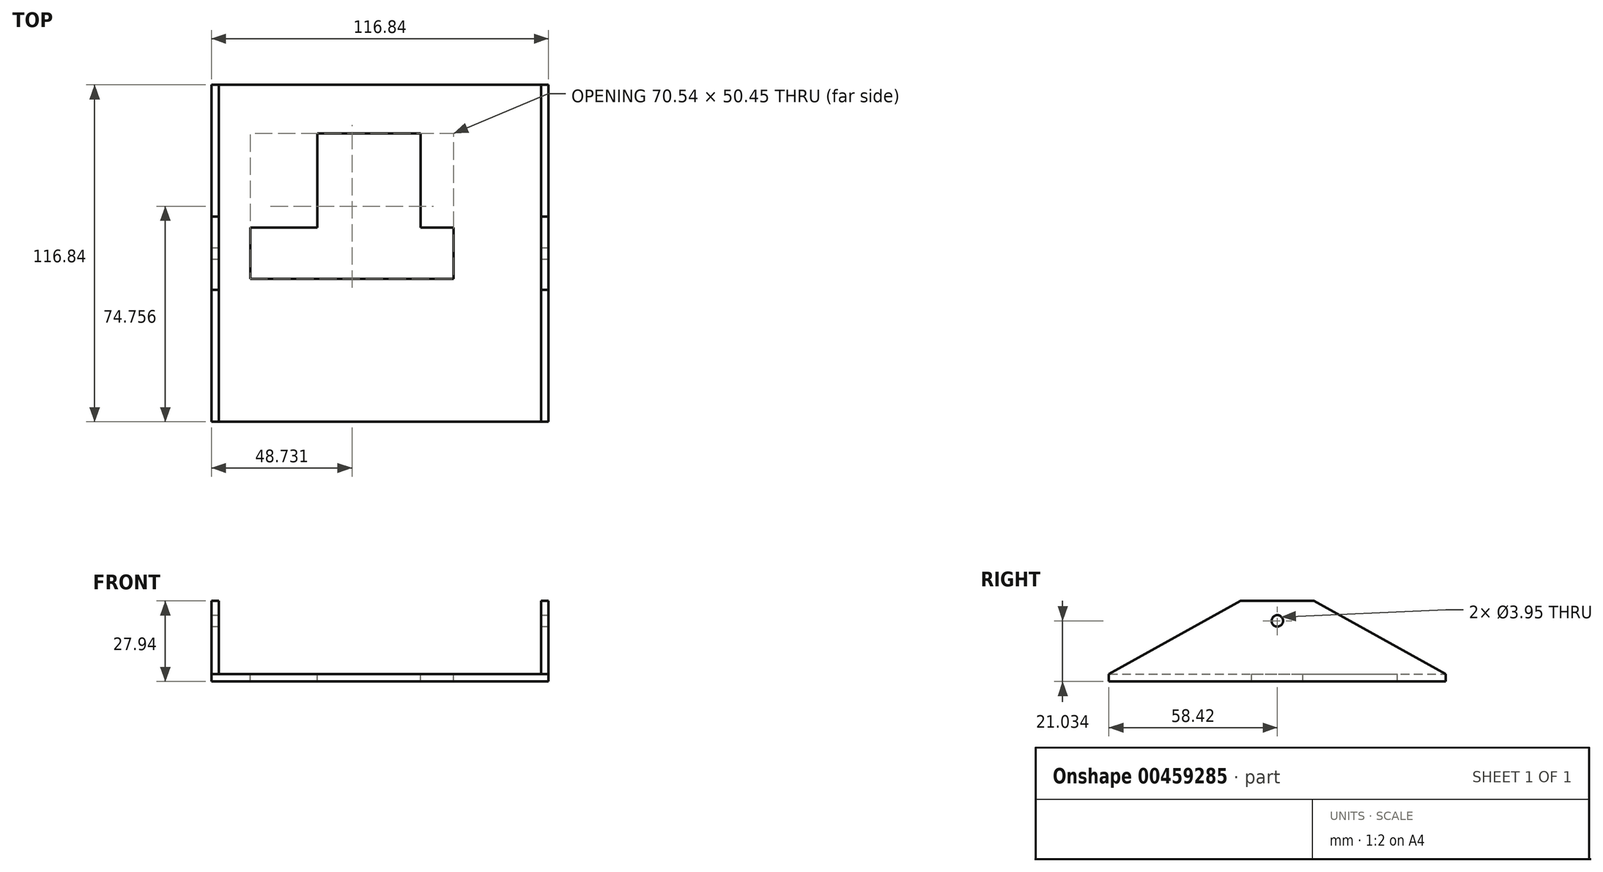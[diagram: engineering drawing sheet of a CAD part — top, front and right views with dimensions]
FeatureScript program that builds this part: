
annotation { "Feature Type Name" : "Feature", "Feature Type Description" : "" }
export const myFeature = defineFeature(function(context is Context, id is Id, definition is map)
    precondition{}
    {
        {
            var Q0;
            Q0=qCreatedBy(makeId("Top.planeOp"),FACE);
            var sketch = newSketch(context, id + "F0", { "sketchPlane" : qUnion([Q0])});
            skLineSegment(sketch, "E0.bottom", {"start": v(58.42, -58.42) * mm, "end": v(-58.42, -58.42) * mm});
            skLineSegment(sketch, "E0.top", {"start": v(58.42, 58.42) * mm, "end": v(-58.42, 58.42) * mm});
            skLineSegment(sketch, "E0.left", {"start": v(58.42, -58.42) * mm, "end": v(58.42, 58.42) * mm});
            skLineSegment(sketch, "E0.right", {"start": v(-58.42, -58.42) * mm, "end": v(-58.42, 58.42) * mm});
            skPoint(sketch, "E0.middle", {"position": v(0, 0) * mm});
            skSolve(sketch);
        }
        {
            var Q0;
            Q0 = qSketchRegion(id + "F0", true);
            extrude(context, id + "F1", {"entities" : qUnion([Q0]), "depth" : 2.54 * mm});
        }
        {
            var Q0;
            Q0=makeQuery(id+"F1.opExtrude","CAP_FACE",FACE,{"disambiguationData":[OSD([sQuery(id+"F0.wireOp",EDGE,"E0.bottom"),sQuery(id+"F0.wireOp",EDGE,"E0.top"),sQuery(id+"F0.wireOp",EDGE,"E0.left"),sQuery(id+"F0.wireOp",EDGE,"E0.right")])],"isStart":false});
            var sketch = newSketch(context, id + "F2", { "sketchPlane" : qUnion([Q0])});
            skLineSegment(sketch, "E1", {"start": v(-55.9, 0) * mm, "end": v(-55.9, 58.42) * mm});
            skLineSegment(sketch, "E2", {"start": v(-55.9, 58.42) * mm, "end": v(-55.9, -58.42) * mm});
            skLineSegment(sketch, "E3", {"start": v(55.89, 0) * mm, "end": v(55.89, -58.42) * mm});
            skLineSegment(sketch, "E4", {"start": v(55.89, -58.42) * mm, "end": v(55.89, 58.42) * mm});
            skSolve(sketch);
        }
        {
            var Q0;
            {var subQ0=makeQuery(id+"F1.opExtrude","CAP_EDGE",EDGE,{"disambiguationData":[OSD([sQuery(id+"F0.wireOp",EDGE,"E0.right")])],"isStart":false});Q0=makeQuery(id+"F2.imprint","IMPRINT",FACE,{"disambiguationData":[TD([[makeQuery(id+"F2.imprint","IMPRINT",EDGE,{"derivedFrom":subQ0}),-1.0]])]});}
            var Q1;
            {var subQ0=makeQuery(id+"F1.opExtrude","CAP_EDGE",EDGE,{"disambiguationData":[OSD([sQuery(id+"F0.wireOp",EDGE,"E0.left")])],"isStart":false});Q1=makeQuery(id+"F2.imprint","IMPRINT",FACE,{"disambiguationData":[TD([[makeQuery(id+"F2.imprint","IMPRINT",EDGE,{"derivedFrom":subQ0}),1.0]])]});}
            extrude(context, id + "F3", {"entities" : qUnion([Q0, Q1]), "operationType" : NewBodyOperationType.ADD, "depth" : 25.4 * mm});
        }
        {
            var Q0;
            Q0=makeQuery(id+"F1.opExtrude","CAP_FACE",FACE,{"disambiguationData":[OSD([sQuery(id+"F0.wireOp",EDGE,"E0.bottom"),sQuery(id+"F0.wireOp",EDGE,"E0.top"),sQuery(id+"F0.wireOp",EDGE,"E0.left"),sQuery(id+"F0.wireOp",EDGE,"E0.right")])],"isStart":false});
            var sketch = newSketch(context, id + "F4", { "sketchPlane" : qUnion([Q0])});
            skLineSegment(sketch, "E5", {"start": v(14.15, 0) * mm, "end": v(14.15, -8.9) * mm});
            skLineSegment(sketch, "E6", {"start": v(14.15, 0) * mm, "end": v(14.15, 8.89) * mm});
            skLineSegment(sketch, "E7", {"start": v(14.15, -8.9) * mm, "end": v(25.58, -8.9) * mm});
            skLineSegment(sketch, "E8", {"start": v(25.58, -8.9) * mm, "end": v(25.58, 8.89) * mm});
            skLineSegment(sketch, "E9", {"start": v(25.58, 8.89) * mm, "end": v(14.15, 8.89) * mm});
            skSolve(sketch);
        }
        {
            var Q0;
            Q0=makeQuery(id+"F4.imprint","IMPRINT",FACE,{"disambiguationData":[TD([[makeQuery(id+"F4.imprint","IMPRINT",EDGE,{"derivedFrom":sQuery(id+"F4.wireOp",EDGE,"E5")}),1.0]])]});
            extrude(context, id + "F5", {"entities" : qUnion([Q0]), "operationType" : NewBodyOperationType.REMOVE, "oppositeDirection" : true, "depth" : 25.4 * mm});
        }
        {
            var Q0;
            {var subQ0=sQuery(id+"F0.wireOp",EDGE,"E0.left");Q0=makeQuery(id+"F3.boolean.opBoolean","MERGE",FACE,{"derivedFrom":[makeQuery(id+"F1.opExtrude","SWEPT_FACE",FACE,{"disambiguationData":[OSD([subQ0])]}),makeQuery(id+"F3.opExtrude","SWEPT_FACE",FACE,{"disambiguationData":[OSD([subQ0])]})]});}
            var sketch = newSketch(context, id + "F6", { "sketchPlane" : qUnion([Q0])});
            skCircle(sketch, "E10", {"center": v(0, 21.03) * mm, "radius": 1.98 * mm});
            skSolve(sketch);
        }
        {
            var Q0;
            Q0=makeQuery(id+"F6.imprint","IMPRINT",FACE,{"disambiguationData":[TD([[makeQuery(id+"F6.imprint","IMPRINT",EDGE,{"derivedFrom":sQuery(id+"F6.wireOp",EDGE,"E10")}),1.0]])]});
            extrude(context, id + "F7", {"entities" : qUnion([Q0]), "operationType" : NewBodyOperationType.REMOVE, "oppositeDirection" : true, "depth" : 141.73 * mm});
        }
        {
            var Q0;
            {var subQ0=sQuery(id+"F0.wireOp",EDGE,"E0.left");Q0=makeQuery(id+"F3.boolean.opBoolean","MERGE",FACE,{"derivedFrom":[makeQuery(id+"F1.opExtrude","SWEPT_FACE",FACE,{"disambiguationData":[OSD([subQ0])]}),makeQuery(id+"F3.opExtrude","SWEPT_FACE",FACE,{"disambiguationData":[OSD([subQ0])]})]});}
            var sketch = newSketch(context, id + "F8", { "sketchPlane" : qUnion([Q0])});
            skLineSegment(sketch, "E11", {"start": v(0, 27.94) * mm, "end": v(-12.7, 27.94) * mm});
            skLineSegment(sketch, "E12", {"start": v(-12.7, 27.94) * mm, "end": v(-58.42, 2.65) * mm});
            skLineSegment(sketch, "E13", {"start": v(0, 27.94) * mm, "end": v(12.7, 27.94) * mm});
            skLineSegment(sketch, "E14", {"start": v(12.7, 27.94) * mm, "end": v(58.42, 2.64) * mm});
            skSolve(sketch);
        }
        {
            var Q0;
            {var subQ0=sQuery(id+"F8.wireOp",EDGE,"E12");Q0=makeQuery(id+"F8.imprint","IMPRINT",FACE,{"disambiguationData":[TD([[makeQuery(id+"F8.imprint","IMPRINT",EDGE,{"derivedFrom":subQ0}),-1.0]])]});}
            var Q1;
            {var subQ0=sQuery(id+"F8.wireOp",EDGE,"E14");Q1=makeQuery(id+"F8.imprint","IMPRINT",FACE,{"disambiguationData":[TD([[makeQuery(id+"F8.imprint","IMPRINT",EDGE,{"derivedFrom":subQ0}),1.0]])]});}
            extrude(context, id + "F9", {"entities" : qUnion([Q0, Q1]), "operationType" : NewBodyOperationType.REMOVE, "oppositeDirection" : true, "depth" : 149.86 * mm});
        }
        {
            var Q0;
            Q0=makeQuery(id+"F1.opExtrude","CAP_FACE",FACE,{"disambiguationData":[OSD([sQuery(id+"F0.wireOp",EDGE,"E0.bottom"),sQuery(id+"F0.wireOp",EDGE,"E0.top"),sQuery(id+"F0.wireOp",EDGE,"E0.left"),sQuery(id+"F0.wireOp",EDGE,"E0.right")])],"isStart":false});
            var sketch = newSketch(context, id + "F10", { "sketchPlane" : qUnion([Q0])});
            skLineSegment(sketch, "E15", {"start": v(14.15, -8.9) * mm, "end": v(-44.96, -8.9) * mm});
            skLineSegment(sketch, "E16", {"start": v(14.15, 8.89) * mm, "end": v(-44.96, 8.89) * mm});
            skLineSegment(sketch, "E17", {"start": v(-44.96, 8.89) * mm, "end": v(-44.96, -8.9) * mm});
            skLineSegment(sketch, "E18", {"start": v(-15.4, 41.56) * mm, "end": v(-9.06, 41.56) * mm});
            skLineSegment(sketch, "E19", {"start": v(-9.06, 41.56) * mm, "end": v(-9.06, 8.89) * mm});
            skLineSegment(sketch, "E20", {"start": v(-15.4, 41.56) * mm, "end": v(-21.75, 41.56) * mm});
            skLineSegment(sketch, "E21", {"start": v(-21.75, 41.56) * mm, "end": v(-21.75, 8.89) * mm});
            skLineSegment(sketch, "E22", {"start": v(14.15, 8.89) * mm, "end": v(14.15, 41.56) * mm});
            skLineSegment(sketch, "E23", {"start": v(14.15, 41.56) * mm, "end": v(-9.06, 41.56) * mm});
            skSolve(sketch);
        }
        {
            var Q0;
            Q0=makeQuery(id+"F10.imprint","IMPRINT",FACE,{"disambiguationData":[TD([[makeQuery(id+"F10.imprint","IMPRINT",EDGE,{"derivedFrom":sQuery(id+"F10.wireOp",EDGE,"E15")}),-1.0]])]});
            var Q1;
            Q1=makeQuery(id+"F10.imprint","IMPRINT",FACE,{"disambiguationData":[TD([[makeQuery(id+"F10.imprint","IMPRINT",EDGE,{"derivedFrom":sQuery(id+"F10.wireOp",EDGE,"E18")}),-1.0]])]});
            extrude(context, id + "F11", {"entities" : qUnion([Q0, Q1]), "operationType" : NewBodyOperationType.REMOVE, "oppositeDirection" : true, "depth" : 25.4 * mm});
        }
        {
            var Q0;
            {var subQ2=sQuery(id+"F10.wireOp",EDGE,"E19");Q0=makeQuery(id+"F10.imprint","IMPRINT",FACE,{"disambiguationData":[TD([[makeQuery(id+"F10.imprint","IMPRINT",EDGE,{"derivedFrom":subQ2}),1.0]])]});}
            extrude(context, id + "F12", {"entities" : qUnion([Q0]), "operationType" : NewBodyOperationType.REMOVE, "oppositeDirection" : true, "depth" : 25.4 * mm});
        }
    });
